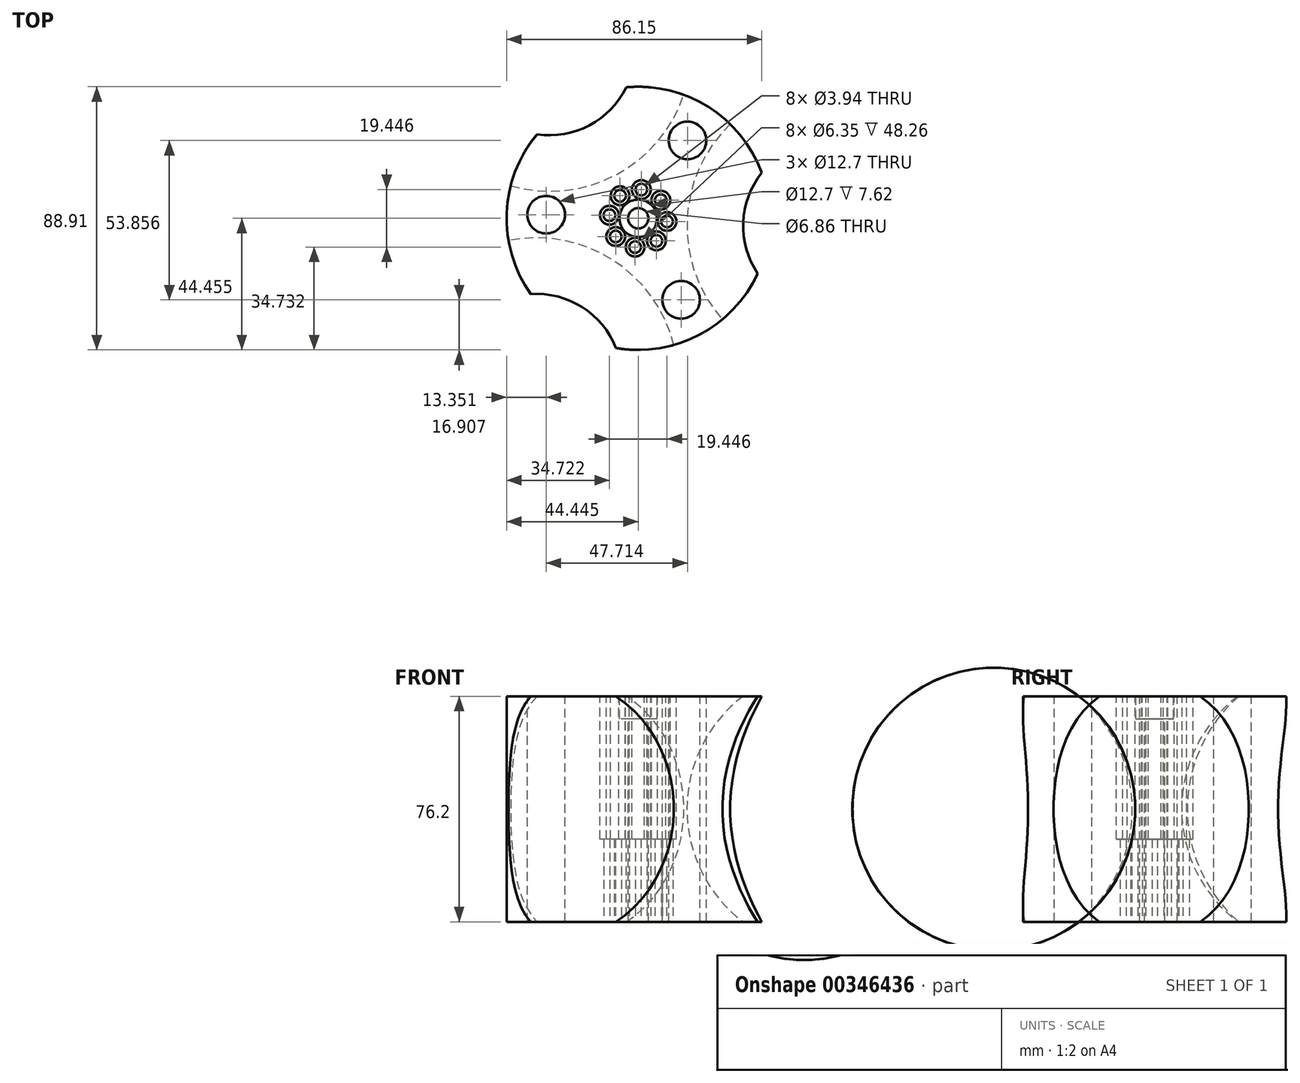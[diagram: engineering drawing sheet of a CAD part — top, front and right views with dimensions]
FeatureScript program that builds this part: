
annotation { "Feature Type Name" : "Feature", "Feature Type Description" : "" }
export const myFeature = defineFeature(function(context is Context, id is Id, definition is map)
    precondition{}
    {
        {
            var Q0;
            Q0=qCreatedBy(makeId("Top.planeOp"),FACE);
            var sketch = newSketch(context, id + "F0", { "sketchPlane" : qUnion([Q0])});
            skCircle(sketch, "E0", {"center": v(-96.8, 47.63) * mm, "radius": 44.45 * mm});
            skCircle(sketch, "E1", {"center": v(-96.8, 47.63) * mm, "radius": 16.51 * mm});
            skCircle(sketch, "E2", {"center": v(-96.8, 47.63) * mm, "radius": 9.78 * mm});
            skCircle(sketch, "E3", {"center": v(-89.18, 53.76) * mm, "radius": 1.97 * mm});
            skCircle(sketch, "E4.1.0", {"center": v(-95.75, 57.35) * mm, "radius": 1.97 * mm});
            skCircle(sketch, "E4.2.0", {"center": v(-102.93, 55.24) * mm, "radius": 1.97 * mm});
            skCircle(sketch, "E4.3.0", {"center": v(-106.52, 48.67) * mm, "radius": 1.97 * mm});
            skCircle(sketch, "E4.4.0", {"center": v(-104.41, 41.5) * mm, "radius": 1.97 * mm});
            skCircle(sketch, "E4.5.0", {"center": v(-97.84, 37.9) * mm, "radius": 1.97 * mm});
            skCircle(sketch, "E4.6.0", {"center": v(-90.66, 40) * mm, "radius": 1.97 * mm});
            skCircle(sketch, "E4.7.0", {"center": v(-87.07, 46.58) * mm, "radius": 1.97 * mm});
            skSolve(sketch);
        }
        {
            var Q0;
            Q0=makeQuery(id+"F0.imprint","IMPRINT",FACE,{"disambiguationData":[TD([[makeQuery(id+"F0.imprint","IMPRINT",EDGE,{"derivedFrom":sQuery(id+"F0.wireOp",EDGE,"E0")}),1.0]])]});
            var Q1;
            Q1=makeQuery(id+"F0.imprint","IMPRINT",FACE,{"disambiguationData":[TD([[makeQuery(id+"F0.imprint","IMPRINT",EDGE,{"derivedFrom":sQuery(id+"F0.wireOp",EDGE,"E1")}),1.0]])]});
            var Q2;
            {var subQ1=sQuery(id+"F0.wireOp",EDGE,"E2");var subQ4=sQuery(id+"F0.wireOp",EDGE,"E3");var subQ5=makeQuery(id+"F0.imprint","INTERSECT",VERTEX,{"disambiguationData":[OD(0.0)],"derivedFrom":[subQ1,subQ4]});Q2=makeQuery(id+"F0.imprint","IMPRINT",FACE,{"disambiguationData":[TD([[makeQuery(id+"F0.imprint","IMPRINT",EDGE,{"disambiguationData":[TD([[subQ5,1.0]])],"derivedFrom":subQ1}),1.0]])]});}
            extrude(context, id + "F1", {"entities" : qUnion([Q0, Q1, Q2]), "depth" : 38.1 * mm, "hasSecondDirection" : true, "secondDirectionOppositeDirection" : true, "secondDirectionDepth" : 38.1 * mm});
        }
        {
            var Q0;
            Q0=qCreatedBy(makeId("Top.planeOp"),FACE);
            var sketch = newSketch(context, id + "F2", { "sketchPlane" : qUnion([Q0])});
            skCircle(sketch, "E5.0.0", {"center": v(-96.8, 47.63) * mm, "radius": 44.45 * mm});
            skCircle(sketch, "E6", {"center": v(-96.8, 47.63) * mm, "radius": 16.51 * mm});
            skLineSegment(sketch, "E7", {"start": v(-107.67, -48.3) * mm, "end": v(-131.12, -6.7) * mm});
            skLineSegment(sketch, "E8", {"start": v(-131.12, -6.7) * mm, "end": v(-154.56, 34.9) * mm});
            skArc(sketch, "E9", {"start": v(-154.56, 34.9) * mm, "mid": v(-172.71, -30.15) * mm, "end": v(-107.67, -48.3) * mm});
            skPoint(sketch, "E10", {"position": v(-80.34, 45.07) * mm});
            skLineSegment(sketch, "E11", {"start": v(-96.8, 47.63) * mm, "end": v(-132.94, -9.59) * mm, "construction": true});
            skLineSegment(sketch, "E12.1.0", {"start": v(-32.58, 45.07) * mm, "end": v(-56.89, 3.96) * mm});
            skArc(sketch, "E12.1.1", {"start": v(-56.89, 3.96) * mm, "mid": v(8.52, 20.77) * mm, "end": v(-8.28, 86.17) * mm});
            skLineSegment(sketch, "E12.1.2", {"start": v(-8.28, 86.17) * mm, "end": v(-32.58, 45.07) * mm});
            skLineSegment(sketch, "E12.2.0", {"start": v(-126.68, 104.51) * mm, "end": v(-78.94, 104.02) * mm});
            skArc(sketch, "E12.2.1", {"start": v(-78.94, 104.02) * mm, "mid": v(-126.2, 152.26) * mm, "end": v(-174.43, 105) * mm});
            skLineSegment(sketch, "E12.2.2", {"start": v(-174.43, 105) * mm, "end": v(-126.68, 104.51) * mm});
            skLineSegment(sketch, "E13", {"start": v(-96.8, 47.63) * mm, "end": v(-89.12, 33) * mm, "construction": true});
            skLineSegment(sketch, "E14", {"start": v(-89.12, 33) * mm, "end": v(-55.1, -31.75) * mm, "construction": true});
            skLineSegment(sketch, "E15", {"start": v(-32.58, 45.07) * mm, "end": v(-80.34, 45.07) * mm, "construction": true});
            skLineSegment(sketch, "E16", {"start": v(-98.9, -50.74) * mm, "end": v(-55.1, -31.75) * mm});
            skLineSegment(sketch, "E17", {"start": v(-55.1, -31.75) * mm, "end": v(-12.82, -9.54) * mm});
            skArc(sketch, "E18", {"start": v(-98.9, -50.74) * mm, "mid": v(-34.47, -74.82) * mm, "end": v(-12.82, -9.54) * mm});
            skArc(sketch, "E19.1.0", {"start": v(-10.55, 94.99) * mm, "mid": v(-21.92, 162.82) * mm, "end": v(-89.28, 148.93) * mm});
            skLineSegment(sketch, "E19.1.1", {"start": v(-10.55, 94.99) * mm, "end": v(-48.9, 123.43) * mm});
            skArc(sketch, "E19.2.0", {"start": v(-180.93, 98.63) * mm, "mid": v(-234, 54.87) * mm, "end": v(-188.29, 3.48) * mm});
            skLineSegment(sketch, "E19.2.1", {"start": v(-180.93, 98.63) * mm, "end": v(-186.39, 51.2) * mm});
            skLineSegment(sketch, "E20", {"start": v(-186.39, 51.2) * mm, "end": v(-188.29, 3.48) * mm});
            skLineSegment(sketch, "E21", {"start": v(-89.28, 148.93) * mm, "end": v(-48.9, 123.43) * mm});
            skSolve(sketch);
        }
        {
            var Q0;
            Q0=makeQuery(id+"F2.imprint","IMPRINT",FACE,{"disambiguationData":[TD([[makeQuery(id+"F2.imprint","IMPRINT",EDGE,{"derivedFrom":sQuery(id+"F2.wireOp",EDGE,"E12.2.0")}),1.0]])]});
            var Q1;
            Q1=sQuery(id+"F2.wireOp",EDGE,"aOpEJ7Df-Mzx5-U4IW-AKo9-5E0Zru6Bx9m7");
            var Q2;
            Q2=sQuery(id+"F2.wireOp",EDGE,"E12.2.2");
            revolve(context, id + "F3", {"operationType" : NewBodyOperationType.REMOVE, "entities" : qUnion([Q0]), "surfaceEntities" : qUnion([Q1]), "axis" : qUnion([Q2]), "revolveType" : RevolveType.FULL, "oppositeDirection" : true});
        }
        {
            var Q0;
            Q0=makeQuery(id+"F2.imprint","IMPRINT",FACE,{"disambiguationData":[TD([[makeQuery(id+"F2.imprint","IMPRINT",EDGE,{"derivedFrom":sQuery(id+"F2.wireOp",EDGE,"E12.1.0")}),1.0]])]});
            var Q1;
            Q1=sQuery(id+"F2.wireOp",EDGE,"E12.1.0");
            revolve(context, id + "F4", {"operationType" : NewBodyOperationType.REMOVE, "entities" : qUnion([Q0]), "axis" : qUnion([Q1]), "revolveType" : RevolveType.FULL, "oppositeDirection" : true});
        }
        {
            var Q0;
            Q0=makeQuery(id+"F2.imprint","IMPRINT",FACE,{"disambiguationData":[TD([[makeQuery(id+"F2.imprint","IMPRINT",EDGE,{"derivedFrom":sQuery(id+"F2.wireOp",EDGE,"E7")}),1.0]])]});
            var Q1;
            Q1=sQuery(id+"F2.wireOp",EDGE,"E7");
            revolve(context, id + "F5", {"operationType" : NewBodyOperationType.REMOVE, "entities" : qUnion([Q0]), "axis" : qUnion([Q1]), "revolveType" : RevolveType.FULL, "oppositeDirection" : true});
        }
        {
            var Q0;
            Q0=makeQuery(id+"F1.opExtrude","CAP_FACE",FACE,{"disambiguationData":[OSD([sQuery(id+"F0.wireOp",EDGE,"E0"),sQuery(id+"F0.wireOp",EDGE,"E3"),sQuery(id+"F0.wireOp",EDGE,"E4.1.0"),sQuery(id+"F0.wireOp",EDGE,"E4.2.0"),sQuery(id+"F0.wireOp",EDGE,"E4.3.0"),sQuery(id+"F0.wireOp",EDGE,"E4.4.0"),sQuery(id+"F0.wireOp",EDGE,"E4.5.0"),sQuery(id+"F0.wireOp",EDGE,"E4.6.0"),sQuery(id+"F0.wireOp",EDGE,"E4.7.0")])],"isStart":false});
            var sketch = newSketch(context, id + "F6", { "sketchPlane" : qUnion([Q0])});
            skCircle(sketch, "E22.0", {"center": v(-102.93, 55.24) * mm, "radius": 1.97 * mm});
            skCircle(sketch, "E23", {"center": v(-102.93, 55.24) * mm, "radius": 3.18 * mm});
            skCircle(sketch, "E24.1.0", {"center": v(-95.75, 57.35) * mm, "radius": 3.18 * mm});
            skCircle(sketch, "E24.2.0", {"center": v(-89.18, 53.76) * mm, "radius": 3.18 * mm});
            skCircle(sketch, "E24.3.0", {"center": v(-87.07, 46.58) * mm, "radius": 3.18 * mm});
            skCircle(sketch, "E24.4.0", {"center": v(-90.66, 40) * mm, "radius": 3.18 * mm});
            skCircle(sketch, "E24.5.0", {"center": v(-97.84, 37.9) * mm, "radius": 3.18 * mm});
            skCircle(sketch, "E24.6.0", {"center": v(-104.41, 41.5) * mm, "radius": 3.18 * mm});
            skCircle(sketch, "E24.7.0", {"center": v(-106.52, 48.67) * mm, "radius": 3.18 * mm});
            skPoint(sketch, "E24.center", {"position": v(-96.8, 47.63) * mm});
            skLineSegment(sketch, "E24.anchor1", {"start": v(-96.8, 47.63) * mm, "end": v(-102.93, 55.24) * mm, "construction": true});
            skLineSegment(sketch, "E24.anchor2", {"start": v(-96.8, 47.63) * mm, "end": v(-106.52, 48.67) * mm, "construction": true});
            skSolve(sketch);
        }
        {
            var Q0;
            Q0=makeQuery(id+"F6.imprint","IMPRINT",FACE,{"disambiguationData":[TD([[makeQuery(id+"F6.imprint","IMPRINT",EDGE,{"derivedFrom":sQuery(id+"F6.wireOp",EDGE,"E22.0")}),-1.0]])]});
            var Q1;
            Q1=makeQuery(id+"F6.imprint","IMPRINT",FACE,{"disambiguationData":[TD([[makeQuery(id+"F6.imprint","IMPRINT",EDGE,{"derivedFrom":sQuery(id+"F6.wireOp",EDGE,"E24.1.0")}),1.0]])]});
            var Q2;
            Q2=makeQuery(id+"F6.imprint","IMPRINT",FACE,{"disambiguationData":[TD([[makeQuery(id+"F6.imprint","IMPRINT",EDGE,{"derivedFrom":sQuery(id+"F6.wireOp",EDGE,"E24.2.0")}),1.0]])]});
            var Q3;
            Q3=makeQuery(id+"F6.imprint","IMPRINT",FACE,{"disambiguationData":[TD([[makeQuery(id+"F6.imprint","IMPRINT",EDGE,{"derivedFrom":sQuery(id+"F6.wireOp",EDGE,"E24.3.0")}),1.0]])]});
            var Q4;
            Q4=makeQuery(id+"F6.imprint","IMPRINT",FACE,{"disambiguationData":[TD([[makeQuery(id+"F6.imprint","IMPRINT",EDGE,{"derivedFrom":sQuery(id+"F6.wireOp",EDGE,"E24.4.0")}),1.0]])]});
            var Q5;
            Q5=makeQuery(id+"F6.imprint","IMPRINT",FACE,{"disambiguationData":[TD([[makeQuery(id+"F6.imprint","IMPRINT",EDGE,{"derivedFrom":sQuery(id+"F6.wireOp",EDGE,"E24.5.0")}),1.0]])]});
            var Q6;
            Q6=makeQuery(id+"F6.imprint","IMPRINT",FACE,{"disambiguationData":[TD([[makeQuery(id+"F6.imprint","IMPRINT",EDGE,{"derivedFrom":sQuery(id+"F6.wireOp",EDGE,"E24.6.0")}),1.0]])]});
            var Q7;
            Q7=makeQuery(id+"F6.imprint","IMPRINT",FACE,{"disambiguationData":[TD([[makeQuery(id+"F6.imprint","IMPRINT",EDGE,{"derivedFrom":sQuery(id+"F6.wireOp",EDGE,"E24.7.0")}),1.0]])]});
            var Q8;
            Q8=sQuery(id+"F6.wireOp",EDGE,"E23");
            var Q9;
            Q9=sQuery(id+"F6.wireOp",EDGE,"E24.1.0");
            var Q10;
            Q10=sQuery(id+"F6.wireOp",EDGE,"E24.2.0");
            var Q11;
            Q11=sQuery(id+"F6.wireOp",EDGE,"E24.3.0");
            var Q12;
            Q12=sQuery(id+"F6.wireOp",EDGE,"E24.4.0");
            var Q13;
            Q13=sQuery(id+"F6.wireOp",EDGE,"E24.5.0");
            var Q14;
            Q14=sQuery(id+"F6.wireOp",EDGE,"E24.6.0");
            var Q15;
            Q15=sQuery(id+"F6.wireOp",EDGE,"E24.7.0");
            extrude(context, id + "F7", {"entities" : qUnion([Q0, Q1, Q2, Q3, Q4, Q5, Q6, Q7]), "operationType" : NewBodyOperationType.REMOVE, "surfaceEntities" : qUnion([Q8, Q9, Q10, Q11, Q12, Q13, Q14, Q15]), "oppositeDirection" : true, "depth" : 48.26 * mm});
        }
        {
            var Q0;
            Q0=makeQuery(id+"F1.opExtrude","CAP_FACE",FACE,{"disambiguationData":[OSD([sQuery(id+"F0.wireOp",EDGE,"E0"),sQuery(id+"F0.wireOp",EDGE,"E3"),sQuery(id+"F0.wireOp",EDGE,"E4.1.0"),sQuery(id+"F0.wireOp",EDGE,"E4.2.0"),sQuery(id+"F0.wireOp",EDGE,"E4.3.0"),sQuery(id+"F0.wireOp",EDGE,"E4.4.0"),sQuery(id+"F0.wireOp",EDGE,"E4.5.0"),sQuery(id+"F0.wireOp",EDGE,"E4.6.0"),sQuery(id+"F0.wireOp",EDGE,"E4.7.0")])],"isStart":false});
            var sketch = newSketch(context, id + "F8", { "sketchPlane" : qUnion([Q0])});
            skCircle(sketch, "E25", {"center": v(-96.8, 47.63) * mm, "radius": 6.35 * mm});
            skSolve(sketch);
        }
        {
            var Q0;
            Q0=qSketchRegion(id+"F8",true);
            extrude(context, id + "F9", {"entities" : qUnion([Q0]), "operationType" : NewBodyOperationType.REMOVE, "oppositeDirection" : true, "depth" : 7.62 * mm});
        }
        {
            var Q0;
            Q0=makeQuery(id+"F9.boolean.opBoolean","COPY",FACE,{"derivedFrom":makeQuery(id+"F9.opExtrude","CAP_FACE",FACE,{"disambiguationData":[OSD([sQuery(id+"F8.wireOp",EDGE,"E25")])],"isStart":false})});
            var sketch = newSketch(context, id + "F10", { "sketchPlane" : qUnion([Q0])});
            skCircle(sketch, "E26", {"center": v(-96.8, 47.63) * mm, "radius": 3.43 * mm});
            skSolve(sketch);
        }
        {
            var Q0;
            Q0=makeQuery(id+"F10.imprint","IMPRINT",FACE,{"disambiguationData":[TD([[makeQuery(id+"F10.imprint","IMPRINT",EDGE,{"derivedFrom":sQuery(id+"F10.wireOp",EDGE,"E26")}),1.0]])]});
            extrude(context, id + "F11", {"entities" : qUnion([Q0]), "operationType" : NewBodyOperationType.REMOVE, "endBound" : BoundingType.UP_TO_NEXT, "oppositeDirection" : true, "depth" : 25.4 * mm});
        }
        {
            var Q0;
            Q0=makeQuery(id+"F1.opExtrude","CAP_FACE",FACE,{"disambiguationData":[OSD([sQuery(id+"F0.wireOp",EDGE,"E0"),sQuery(id+"F0.wireOp",EDGE,"E3"),sQuery(id+"F0.wireOp",EDGE,"E4.1.0"),sQuery(id+"F0.wireOp",EDGE,"E4.2.0"),sQuery(id+"F0.wireOp",EDGE,"E4.3.0"),sQuery(id+"F0.wireOp",EDGE,"E4.4.0"),sQuery(id+"F0.wireOp",EDGE,"E4.5.0"),sQuery(id+"F0.wireOp",EDGE,"E4.6.0"),sQuery(id+"F0.wireOp",EDGE,"E4.7.0")])],"isStart":false});
            var sketch = newSketch(context, id + "F12", { "sketchPlane" : qUnion([Q0])});
            skLineSegment(sketch, "E27", {"start": v(-96.8, 47.63) * mm, "end": v(-73.05, 85.2) * mm});
            skCircle(sketch, "E28", {"center": v(-80.17, 73.93) * mm, "radius": 6.35 * mm});
            skCircle(sketch, "E29.1.0", {"center": v(-127.89, 48.86) * mm, "radius": 6.35 * mm});
            skCircle(sketch, "E29.2.0", {"center": v(-82.32, 20.08) * mm, "radius": 6.35 * mm});
            skPoint(sketch, "E29.center", {"position": v(-96.8, 47.63) * mm});
            skSolve(sketch);
        }
        {
            var Q0;
            Q0=makeQuery(id+"F12.imprint","IMPRINT",FACE,{"disambiguationData":[TD([[makeQuery(id+"F12.imprint","IMPRINT",EDGE,{"derivedFrom":sQuery(id+"F12.wireOp",EDGE,"E29.1.0")}),1.0]])]});
            var Q1;
            {var subQ0=sQuery(id+"F12.wireOp",EDGE,"E28");var subQ1=sQuery(id+"F12.wireOp",EDGE,"E27");var subQ2=makeQuery(id+"F12.imprint","INTERSECT",VERTEX,{"disambiguationData":[OD(0.0)],"derivedFrom":[subQ1,subQ0]});Q1=makeQuery(id+"F12.imprint","IMPRINT",FACE,{"disambiguationData":[TD([[makeQuery(id+"F12.imprint","IMPRINT",EDGE,{"disambiguationData":[TD([[subQ2,-1.0]])],"derivedFrom":subQ1}),1.0]])]});}
            var Q2;
            {var subQ0=sQuery(id+"F12.wireOp",EDGE,"E28");var subQ1=sQuery(id+"F12.wireOp",EDGE,"E27");var subQ2=makeQuery(id+"F12.imprint","INTERSECT",VERTEX,{"disambiguationData":[OD(0.0)],"derivedFrom":[subQ1,subQ0]});Q2=makeQuery(id+"F12.imprint","IMPRINT",FACE,{"disambiguationData":[TD([[makeQuery(id+"F12.imprint","IMPRINT",EDGE,{"disambiguationData":[TD([[subQ2,-1.0]])],"derivedFrom":subQ1}),-1.0]])]});}
            var Q3;
            Q3=makeQuery(id+"F12.imprint","IMPRINT",FACE,{"disambiguationData":[TD([[makeQuery(id+"F12.imprint","IMPRINT",EDGE,{"derivedFrom":sQuery(id+"F12.wireOp",EDGE,"E29.2.0")}),1.0]])]});
            extrude(context, id + "F13", {"entities" : qUnion([Q0, Q1, Q2, Q3]), "operationType" : NewBodyOperationType.REMOVE, "endBound" : BoundingType.UP_TO_NEXT, "oppositeDirection" : true, "depth" : 25.4 * mm});
        }
    });
